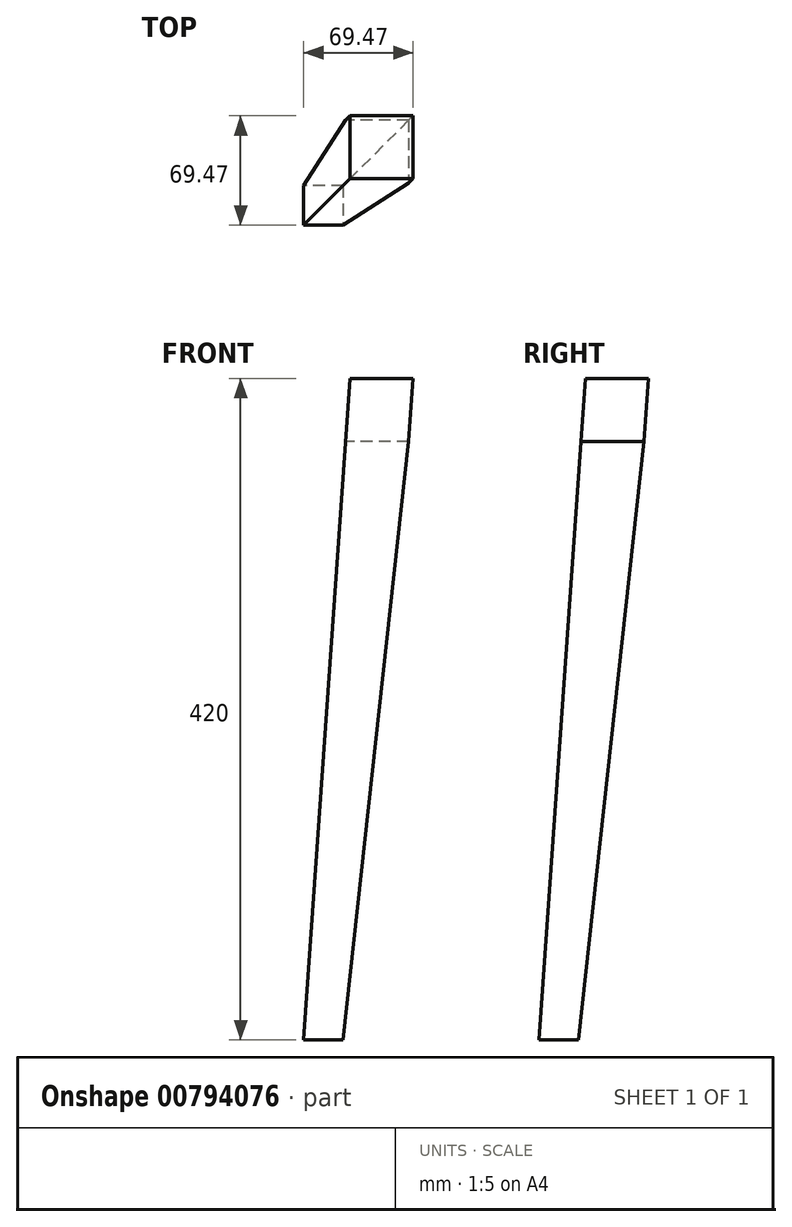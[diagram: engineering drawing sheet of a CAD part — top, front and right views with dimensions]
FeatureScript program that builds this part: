
annotation { "Feature Type Name" : "Feature", "Feature Type Description" : "" }
export const myFeature = defineFeature(function(context is Context, id is Id, definition is map)
    precondition{}
    {
        {
            var Q0;
            Q0=qCreatedBy(makeId("Front.planeOp"),FACE);
            var sketch = newSketch(context, id + "F0", { "sketchPlane" : qUnion([Q0])});
            skLineSegment(sketch, "E0", {"start": v(0, 0) * mm, "end": v(0, 420) * mm, "construction": true});
            skLineSegment(sketch, "E1", {"start": v(0, 0) * mm, "end": v(14.19, 202.91) * mm, "construction": true});
            skLineSegment(sketch, "E2", {"start": v(0, 420) * mm, "end": v(183.53, 420) * mm, "construction": true});
            skLineSegment(sketch, "E3", {"start": v(0, 0) * mm, "end": v(185.43, 0) * mm, "construction": true});
            skLineSegment(sketch, "E4", {"start": v(0, 0) * mm, "end": v(29.88, 427.3) * mm});
            skLineSegment(sketch, "E5", {"start": v(39.9, -2.8) * mm, "end": v(40.1, 0) * mm});
            skLineSegment(sketch, "E6", {"start": v(69.47, 420) * mm, "end": v(69.47, 380) * mm, "construction": true});
            skLineSegment(sketch, "E7", {"start": v(69.47, 380) * mm, "end": v(14.52, 380) * mm, "construction": true});
            skLineSegment(sketch, "E8", {"start": v(0, 0) * mm, "end": v(25, 0) * mm});
            skLineSegment(sketch, "E9", {"start": v(25, 0) * mm, "end": v(66.67, 380) * mm});
            skLineSegment(sketch, "E10.trimOffspring", {"start": v(66.67, 380) * mm, "end": v(70.77, 438.64) * mm});
            skLineSegment(sketch, "E11", {"start": v(29.37, 420) * mm, "end": v(69.47, 420) * mm});
            skSolve(sketch);
        }
        {
            var Q0;
            Q0 = qSketchRegion(id + "F0", true);
            extrude(context, id + "F1", {"entities" : qUnion([Q0]), "oppositeDirection" : true, "depth" : 70 * mm, "offsetDistance" : 25 * mm});
        }
        {
            var Q0;
            Q0=qCreatedBy(makeId("Right.planeOp"),FACE);
            var sketch = newSketch(context, id + "F2", { "sketchPlane" : qUnion([Q0])});
            skLineSegment(sketch, "E12", {"start": v(0, 0) * mm, "end": v(0, 420) * mm, "construction": true});
            skLineSegment(sketch, "E13", {"start": v(0, 420) * mm, "end": v(156.94, 420) * mm, "construction": true});
            skLineSegment(sketch, "E14", {"start": v(0, 0) * mm, "end": v(141.15, 0) * mm, "construction": true});
            skLineSegment(sketch, "E15", {"start": v(0, 0) * mm, "end": v(29.37, 420) * mm});
            skLineSegment(sketch, "E16", {"start": v(25, 0) * mm, "end": v(66.67, 380) * mm});
            skLineSegment(sketch, "E17.trimOffspring", {"start": v(66.67, 380) * mm, "end": v(69.47, 420) * mm});
            skLineSegment(sketch, "E18", {"start": v(0, 0) * mm, "end": v(0, 420) * mm});
            skLineSegment(sketch, "E19", {"start": v(0, 420) * mm, "end": v(29.37, 420) * mm});
            skLineSegment(sketch, "E20", {"start": v(69.47, 420) * mm, "end": v(73.1, 420) * mm});
            skLineSegment(sketch, "E21", {"start": v(73.1, 420) * mm, "end": v(81.18, -12.98) * mm});
            skLineSegment(sketch, "E22", {"start": v(81.18, -12.98) * mm, "end": v(25, 0) * mm});
            skSolve(sketch);
        }
        {
            var Q0;
            Q0 = qSketchRegion(id + "F2", true);
            extrude(context, id + "F3", {"entities" : qUnion([Q0]), "operationType" : NewBodyOperationType.REMOVE, "depth" : 240 * mm, "offsetDistance" : 25 * mm});
        }
    });
